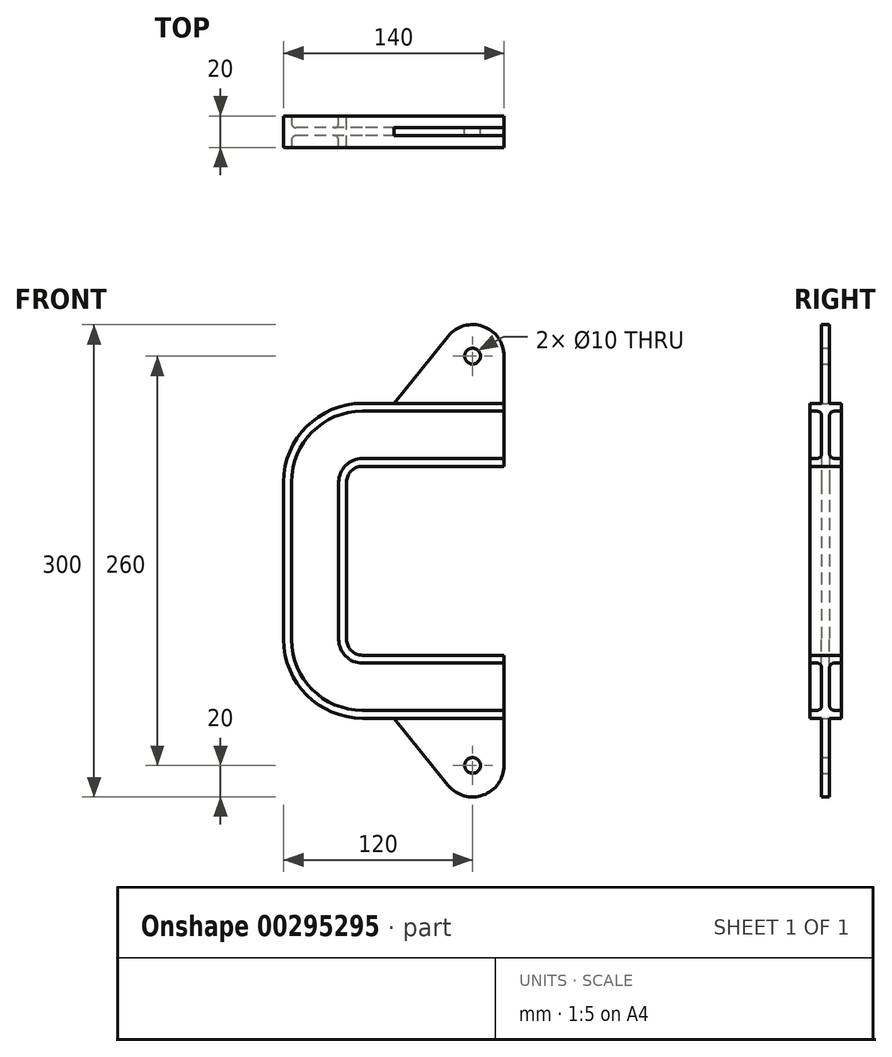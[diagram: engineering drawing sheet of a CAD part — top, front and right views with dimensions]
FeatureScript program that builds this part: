
annotation { "Feature Type Name" : "Feature", "Feature Type Description" : "" }
export const myFeature = defineFeature(function(context is Context, id is Id, definition is map)
    precondition{}
    {
        {
            var Q0;
            Q0=qCreatedBy(makeId("Front.planeOp"),FACE);
            var sketch = newSketch(context, id + "F0", { "sketchPlane" : qUnion([Q0])});
            skLineSegment(sketch, "E0", {"start": v(0, 60) * mm, "end": v(-90, 60) * mm});
            skArc(sketch, "E1", {"start": v(-90, 60) * mm, "mid": v(-97.07, 57.07) * mm, "end": v(-100, 50) * mm});
            skLineSegment(sketch, "E2", {"start": v(-100, 50) * mm, "end": v(-100, 0) * mm});
            skSolve(sketch);
        }
        {
            var Q0;
            Q0=qCreatedBy(makeId("Right.planeOp"),FACE);
            var sketch = newSketch(context, id + "F1", { "sketchPlane" : qUnion([Q0])});
            skLineSegment(sketch, "E3", {"start": v(-10, 95) * mm, "end": v(-10, 100) * mm});
            skLineSegment(sketch, "E4", {"start": v(-10, 100) * mm, "end": v(10, 100) * mm});
            skLineSegment(sketch, "E5", {"start": v(10, 100) * mm, "end": v(10, 95) * mm});
            skLineSegment(sketch, "E6", {"start": v(10, 95) * mm, "end": v(5.5, 95) * mm});
            skLineSegment(sketch, "E7", {"start": v(2.5, 92) * mm, "end": v(2.5, 68) * mm});
            skLineSegment(sketch, "E8", {"start": v(5.5, 65) * mm, "end": v(10, 65) * mm});
            skLineSegment(sketch, "E9", {"start": v(10, 65) * mm, "end": v(10, 60) * mm});
            skLineSegment(sketch, "E10", {"start": v(-10, 60) * mm, "end": v(-10, 65) * mm});
            skLineSegment(sketch, "E11", {"start": v(-10, 65) * mm, "end": v(-5.5, 65) * mm});
            skLineSegment(sketch, "E12", {"start": v(-2.5, 68) * mm, "end": v(-2.5, 92) * mm});
            skLineSegment(sketch, "E13", {"start": v(-5.5, 95) * mm, "end": v(-10, 95) * mm});
            skPoint(sketch, "E14.visualSharp", {"position": v(2.5, 95) * mm});
            skArc(sketch, "E14.filletArc", {"start": v(5.5, 95) * mm, "mid": v(3.38, 94.12) * mm, "end": v(2.5, 92) * mm});
            skPoint(sketch, "E15.visualSharp", {"position": v(2.5, 65) * mm});
            skArc(sketch, "E15.filletArc", {"start": v(2.5, 68) * mm, "mid": v(3.38, 65.88) * mm, "end": v(5.5, 65) * mm});
            skPoint(sketch, "E16.visualSharp", {"position": v(-2.5, 65) * mm});
            skArc(sketch, "E16.filletArc", {"start": v(-5.5, 65) * mm, "mid": v(-3.38, 65.88) * mm, "end": v(-2.5, 68) * mm});
            skPoint(sketch, "E17.visualSharp", {"position": v(-2.5, 95) * mm});
            skArc(sketch, "E17.filletArc", {"start": v(-2.5, 92) * mm, "mid": v(-3.38, 94.12) * mm, "end": v(-5.5, 95) * mm});
            skLineSegment(sketch, "E18", {"start": v(-10, 60) * mm, "end": v(0, 60) * mm});
            skLineSegment(sketch, "E19", {"start": v(0, 60) * mm, "end": v(10, 60) * mm});
            skSolve(sketch);
        }
        {
            var Q0;
            Q0=makeQuery(id+"F1.imprint","IMPRINT",FACE,{"disambiguationData":[TD([[makeQuery(id+"F1.imprint","IMPRINT",EDGE,{"derivedFrom":sQuery(id+"F1.wireOp",EDGE,"E3")}),-1.0]])]});
            var Q1;
            Q1=sQuery(id+"F0.wireOp",EDGE,"E0");
            var Q2;
            Q2=sQuery(id+"F0.wireOp",EDGE,"E1");
            var Q3;
            Q3=sQuery(id+"F0.wireOp",EDGE,"E2");
            sweep(context, id + "F2", {"profiles" : qUnion([Q0]), "path" : qUnion([Q1, Q2, Q3])});
        }
        {
            var Q0;
            Q0=makeQuery(id+"F2.opSweep","SWEPT_BODY",BODY,{"disambiguationData":[OSD([sQuery(id+"F0.wireOp",EDGE,"E2"),sQuery(id+"F1.wireOp",EDGE,"E3"),sQuery(id+"F1.wireOp",EDGE,"E4"),sQuery(id+"F1.wireOp",EDGE,"E5"),sQuery(id+"F1.wireOp",EDGE,"E6"),sQuery(id+"F1.wireOp",EDGE,"E7"),sQuery(id+"F1.wireOp",EDGE,"E8"),sQuery(id+"F1.wireOp",EDGE,"E9"),sQuery(id+"F1.wireOp",EDGE,"E10"),sQuery(id+"F1.wireOp",EDGE,"E11"),sQuery(id+"F1.wireOp",EDGE,"E12"),sQuery(id+"F1.wireOp",EDGE,"E13"),sQuery(id+"F1.wireOp",EDGE,"E14.filletArc"),sQuery(id+"F1.wireOp",EDGE,"E15.filletArc"),sQuery(id+"F1.wireOp",EDGE,"E16.filletArc"),sQuery(id+"F1.wireOp",EDGE,"E17.filletArc"),sQuery(id+"F1.wireOp",EDGE,"E18"),sQuery(id+"F1.wireOp",EDGE,"E19")])]});
            var Q1;
            Q1=qCreatedBy(makeId("Top.planeOp"),FACE);
            mirror(context, id + "F3", {"operationType" : NewBodyOperationType.ADD, "entities" : qUnion([Q0]), "mirrorPlane" : qUnion([Q1])});
        }
        {
            var Q0;
            Q0=qCreatedBy(makeId("Front.planeOp"),FACE);
            var sketch = newSketch(context, id + "F4", { "sketchPlane" : qUnion([Q0])});
            skLineSegment(sketch, "E20", {"start": v(-70, 100) * mm, "end": v(0, 100) * mm});
            skLineSegment(sketch, "E21", {"start": v(0, 100) * mm, "end": v(0, 130) * mm});
            skLineSegment(sketch, "E22", {"start": v(-35.55, 142.58) * mm, "end": v(-70, 100) * mm});
            skArc(sketch, "E23.filletArc", {"start": v(0, 130) * mm, "mid": v(-13.33, 148.85) * mm, "end": v(-35.55, 142.58) * mm});
            skCircle(sketch, "E24", {"center": v(-20, 130) * mm, "radius": 5 * mm});
            skLineSegment(sketch, "E25.MirrorCS", {"start": v(-70, -100) * mm, "end": v(0, -100) * mm});
            skLineSegment(sketch, "E26.MirrorCS", {"start": v(-35.55, -142.58) * mm, "end": v(-70, -100) * mm});
            skArc(sketch, "E27.MirrorCS", {"start": v(0, -130) * mm, "mid": v(-13.33, -148.85) * mm, "end": v(-35.55, -142.58) * mm});
            skLineSegment(sketch, "E28.MirrorCS", {"start": v(0, -100) * mm, "end": v(0, -130) * mm});
            skCircle(sketch, "E29.MirrorC", {"center": v(-20, -130) * mm, "radius": 5 * mm});
            skSolve(sketch);
        }
        {
            var Q0;
            Q0=makeQuery(id+"F4.imprint","IMPRINT",FACE,{"disambiguationData":[TD([[makeQuery(id+"F4.imprint","IMPRINT",EDGE,{"derivedFrom":sQuery(id+"F4.wireOp",EDGE,"E20")}),1.0]])]});
            var Q1;
            Q1=makeQuery(id+"F4.imprint","IMPRINT",FACE,{"disambiguationData":[TD([[makeQuery(id+"F4.imprint","IMPRINT",EDGE,{"derivedFrom":sQuery(id+"F4.wireOp",EDGE,"E25.MirrorCS")}),-1.0]])]});
            extrude(context, id + "F5", {"entities" : qUnion([Q0, Q1]), "operationType" : NewBodyOperationType.ADD, "endBound" : BoundingType.SYMMETRIC, "depth" : 5 * mm});
        }
    });
